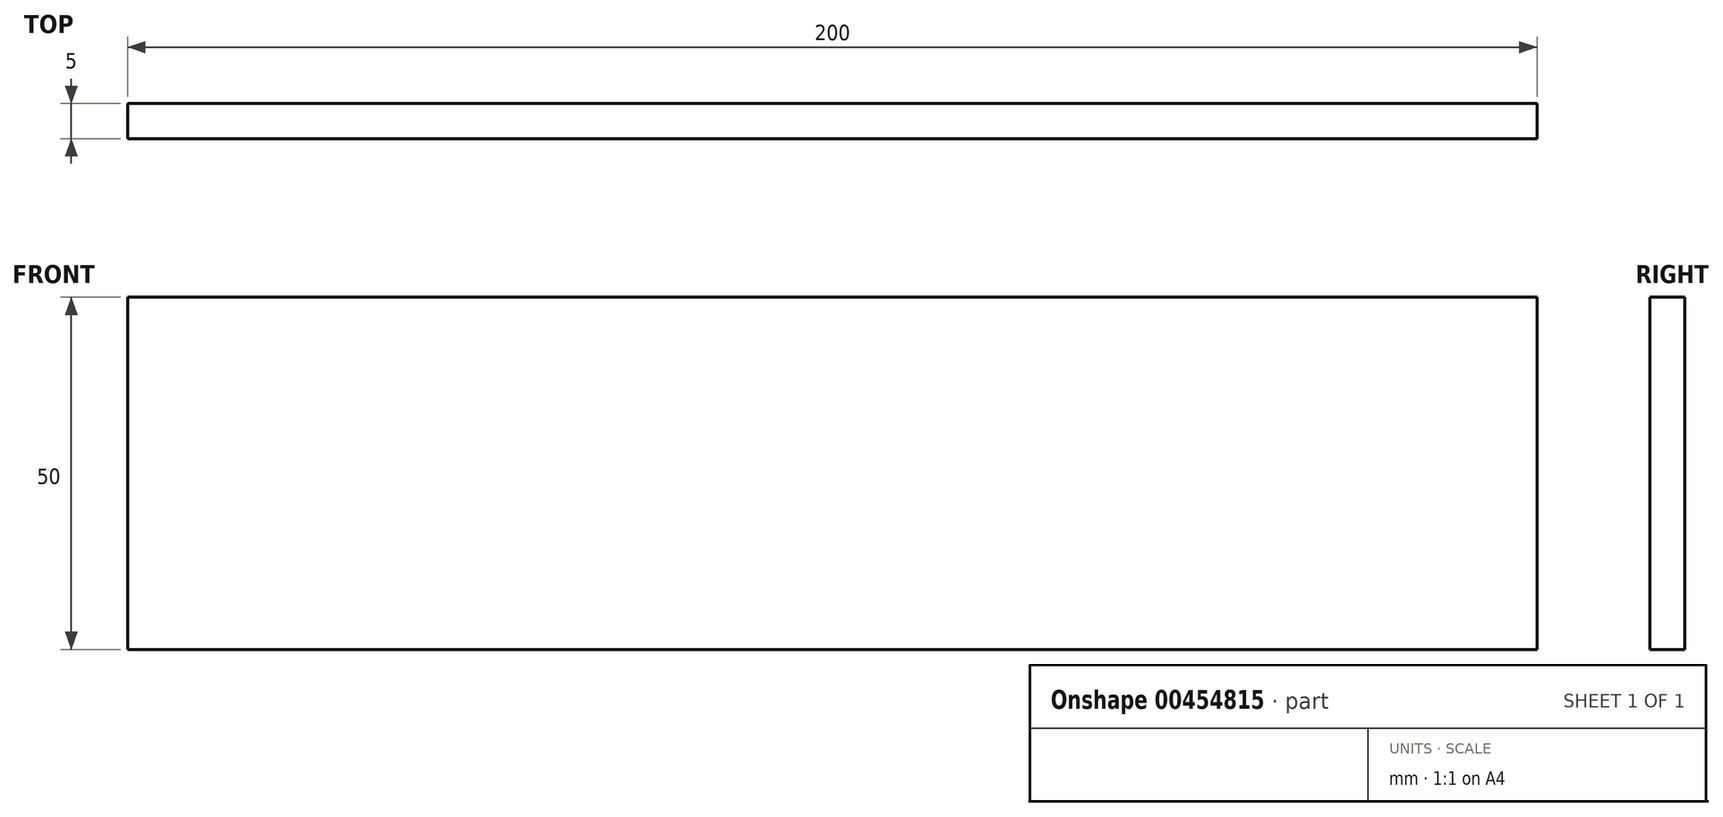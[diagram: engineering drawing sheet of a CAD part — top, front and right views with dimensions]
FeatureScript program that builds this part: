
annotation { "Feature Type Name" : "Feature", "Feature Type Description" : "" }
export const myFeature = defineFeature(function(context is Context, id is Id, definition is map)
    precondition{}
    {
        {
            var Q0;
            Q0=qCreatedBy(makeId("Front.planeOp"),FACE);
            var sketch = newSketch(context, id + "F0", { "sketchPlane" : qUnion([Q0])});
            skLineSegment(sketch, "E0.bottom", {"start": v(100, -25) * mm, "end": v(-100, -25) * mm});
            skLineSegment(sketch, "E0.top", {"start": v(100, 25) * mm, "end": v(-100, 25) * mm});
            skLineSegment(sketch, "E0.left", {"start": v(100, -25) * mm, "end": v(100, 25) * mm});
            skLineSegment(sketch, "E0.right", {"start": v(-100, -25) * mm, "end": v(-100, 25) * mm});
            skPoint(sketch, "E0.middle", {"position": v(0, 0) * mm});
            skSolve(sketch);
        }
        {
            var Q0;
            Q0 = qSketchRegion(id + "F0", true);
            extrude(context, id + "F1", {"entities" : qUnion([Q0]), "depth" : 5 * mm});
        }
    });
